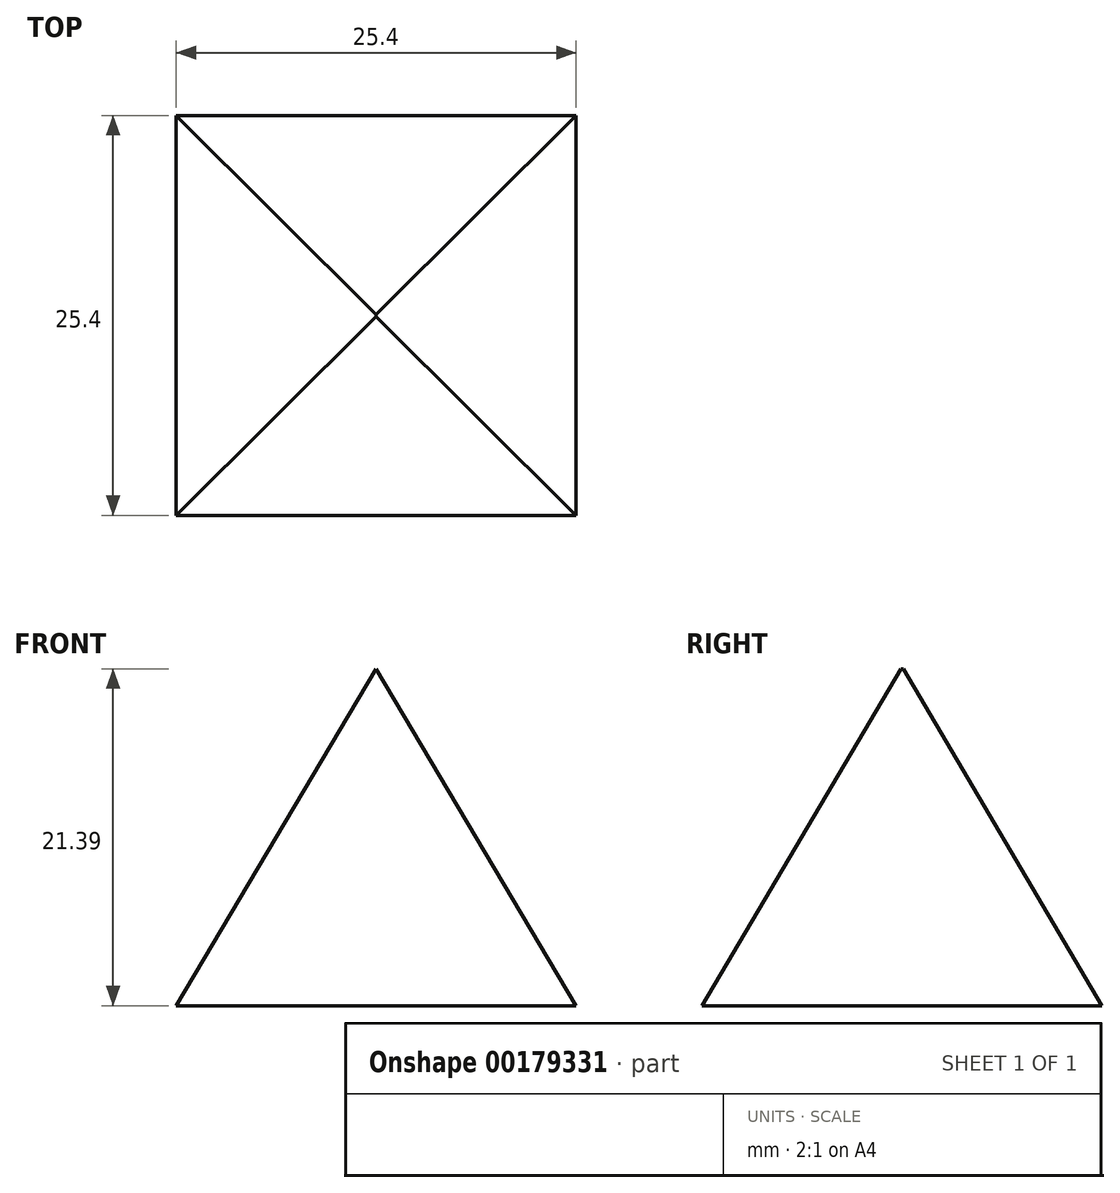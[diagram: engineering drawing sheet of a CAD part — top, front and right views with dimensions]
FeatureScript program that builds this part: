
annotation { "Feature Type Name" : "Feature", "Feature Type Description" : "" }
export const myFeature = defineFeature(function(context is Context, id is Id, definition is map)
    precondition{}
    {
        {
            var Q0;
            Q0=qCreatedBy(makeId("Front.planeOp"),FACE);
            var sketch = newSketch(context, id + "F0", { "sketchPlane" : qUnion([Q0])});
            skLineSegment(sketch, "E0", {"start": v(0, 0) * mm, "end": v(12.7, 21.4) * mm});
            skLineSegment(sketch, "E1", {"start": v(12.7, 21.4) * mm, "end": v(25.4, 0) * mm});
            skLineSegment(sketch, "E2", {"start": v(25.4, 0) * mm, "end": v(0, 0) * mm});
            skSolve(sketch);
        }
        {
            var Q0;
            Q0=makeQuery(id+"F0.imprint","IMPRINT",FACE,{"disambiguationData":[TD([[makeQuery(id+"F0.imprint","IMPRINT",EDGE,{"derivedFrom":sQuery(id+"F0.wireOp",EDGE,"E0")}),-1.0]])]});
            extrude(context, id + "F1", {"entities" : qUnion([Q0]), "depth" : 25.4 * mm});
        }
        {
            var Q0;
            Q0=qCreatedBy(makeId("Right.planeOp"),FACE);
            var sketch = newSketch(context, id + "F2", { "sketchPlane" : qUnion([Q0])});
            skLineSegment(sketch, "E3", {"start": v(0, 0) * mm, "end": v(-12.7, 21.52) * mm});
            skLineSegment(sketch, "E4", {"start": v(-12.7, 21.52) * mm, "end": v(-25.4, 0) * mm});
            skLineSegment(sketch, "E5", {"start": v(-25.4, 0) * mm, "end": v(0, 0) * mm});
            skLineSegment(sketch, "E6.bottom", {"start": v(0, 0) * mm, "end": v(-25.4, 0) * mm});
            skLineSegment(sketch, "E6.top", {"start": v(0, 21.52) * mm, "end": v(-25.4, 21.52) * mm});
            skLineSegment(sketch, "E6.left", {"start": v(0, 0) * mm, "end": v(0, 21.52) * mm});
            skLineSegment(sketch, "E6.right", {"start": v(-25.4, 0) * mm, "end": v(-25.4, 21.52) * mm});
            skSolve(sketch);
        }
        {
            var Q0;
            {var subQ0=sQuery(id+"F2.wireOp",EDGE,"E6.left");Q0=makeQuery(id+"F2.imprint","IMPRINT",FACE,{"disambiguationData":[TD([[makeQuery(id+"F2.imprint","IMPRINT",EDGE,{"derivedFrom":subQ0}),1.0]])]});}
            var Q1;
            {var subQ0=sQuery(id+"F2.wireOp",EDGE,"E6.right");Q1=makeQuery(id+"F2.imprint","IMPRINT",FACE,{"disambiguationData":[TD([[makeQuery(id+"F2.imprint","IMPRINT",EDGE,{"derivedFrom":subQ0}),-1.0]])]});}
            extrude(context, id + "F3", {"entities" : qUnion([Q0, Q1]), "operationType" : NewBodyOperationType.REMOVE, "depth" : 25.4 * mm});
        }
    });
